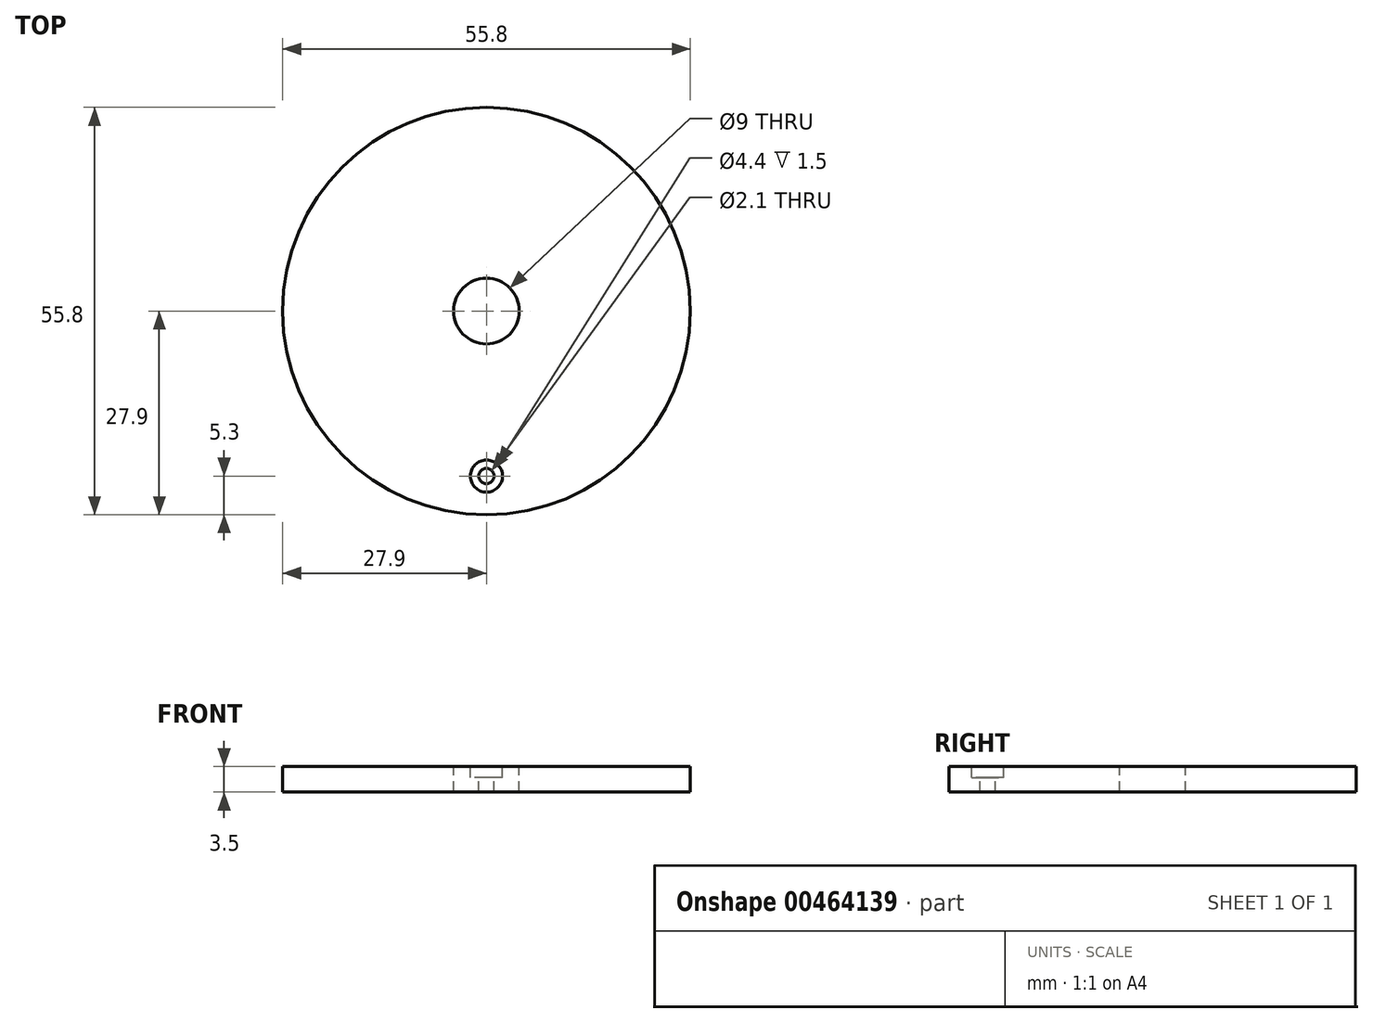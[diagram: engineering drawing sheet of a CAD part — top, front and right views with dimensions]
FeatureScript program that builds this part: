
annotation { "Feature Type Name" : "Feature", "Feature Type Description" : "" }
export const myFeature = defineFeature(function(context is Context, id is Id, definition is map)
    precondition{}
    {
        {
            var Q0;
            Q0=qCreatedBy(makeId("Top.planeOp"),FACE);
            var sketch = newSketch(context, id + "F0", { "sketchPlane" : qUnion([Q0])});
            skCircle(sketch, "E0", {"center": v(0, 0) * mm, "radius": 22.6 * mm, "construction": true});
            skCircle(sketch, "E1", {"center": v(0, 0) * mm, "radius": 27.9 * mm});
            skPoint(sketch, "E2", {"position": v(0, -22.6) * mm});
            skCircle(sketch, "E3", {"center": v(0, -22.6) * mm, "radius": 2.2 * mm});
            skCircle(sketch, "E4", {"center": v(0, -22.6) * mm, "radius": 1.05 * mm});
            skCircle(sketch, "E5", {"center": v(0, 0) * mm, "radius": 4.5 * mm});
            skSolve(sketch);
        }
        {
            var Q0;
            Q0=qSketchRegion(id+"F0",true);
            var Q1;
            Q1=makeQuery(id+"F0.imprint","IMPRINT",FACE,{"disambiguationData":[TD([[makeQuery(id+"F0.imprint","IMPRINT",EDGE,{"derivedFrom":sQuery(id+"F0.wireOp",EDGE,"E3")}),1.0]])]});
            var Q2;
            Q2=makeQuery(id+"F0.imprint","IMPRINT",FACE,{"disambiguationData":[TD([[makeQuery(id+"F0.imprint","IMPRINT",EDGE,{"derivedFrom":sQuery(id+"F0.wireOp",EDGE,"E4")}),1.0]])]});
            extrude(context, id + "F1", {"entities" : qUnion([Q0, Q1, Q2]), "oppositeDirection" : true, "depth" : 3.5 * mm});
        }
        {
            var Q0;
            Q0=makeQuery(id+"F0.imprint","IMPRINT",FACE,{"disambiguationData":[TD([[makeQuery(id+"F0.imprint","IMPRINT",EDGE,{"derivedFrom":sQuery(id+"F0.wireOp",EDGE,"E4")}),1.0]])]});
            var Q1;
            Q1=makeQuery(id+"F0.imprint","IMPRINT",FACE,{"disambiguationData":[TD([[makeQuery(id+"F0.imprint","IMPRINT",EDGE,{"derivedFrom":sQuery(id+"F0.wireOp",EDGE,"E3")}),1.0]])]});
            extrude(context, id + "F2", {"entities" : qUnion([Q0, Q1]), "operationType" : NewBodyOperationType.REMOVE, "oppositeDirection" : true, "depth" : 1.5 * mm});
        }
        {
            var Q0;
            Q0=makeQuery(id+"F0.imprint","IMPRINT",FACE,{"disambiguationData":[TD([[makeQuery(id+"F0.imprint","IMPRINT",EDGE,{"derivedFrom":sQuery(id+"F0.wireOp",EDGE,"E4")}),1.0]])]});
            var Q1;
            Q1=makeQuery(id+"F1.opExtrude","CAP_FACE",FACE,{"disambiguationData":[OSD([sQuery(id+"F0.wireOp",EDGE,"E1")])],"isStart":false});
            extrude(context, id + "F3", {"entities" : qUnion([Q0]), "operationType" : NewBodyOperationType.REMOVE, "endBound" : BoundingType.UP_TO_SURFACE, "oppositeDirection" : true, "endBoundEntityFace" : qUnion([Q1]), "depth" : 25 * mm});
        }
    });
